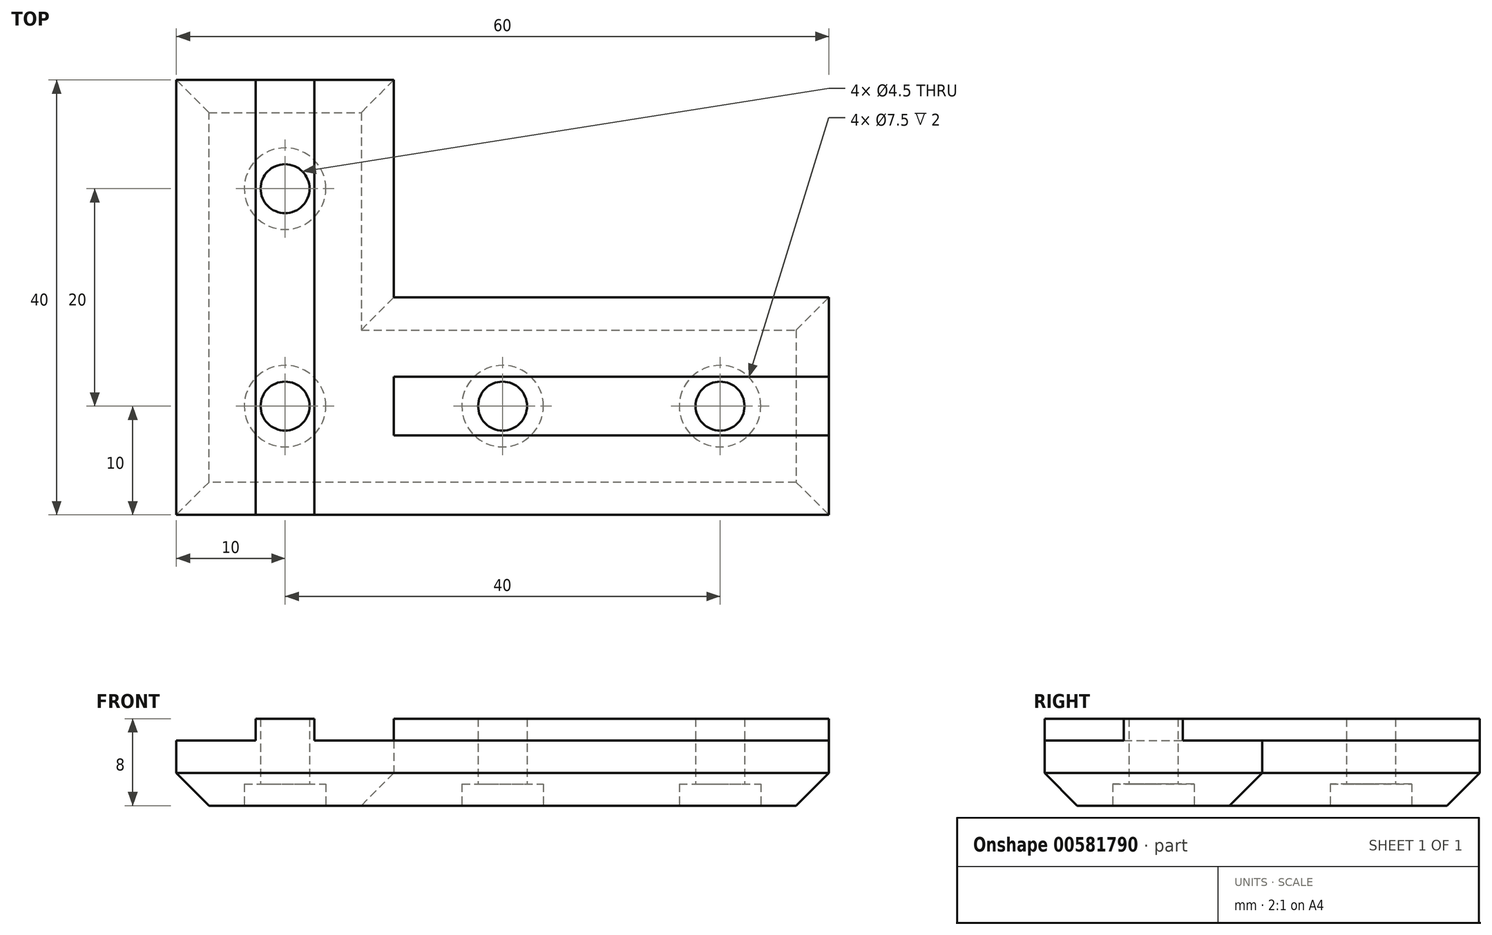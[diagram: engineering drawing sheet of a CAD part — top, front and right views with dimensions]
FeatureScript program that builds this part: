
annotation { "Feature Type Name" : "Feature", "Feature Type Description" : "" }
export const myFeature = defineFeature(function(context is Context, id is Id, definition is map)
    precondition{}
    {
        {
            var Q0;
            Q0=qCreatedBy(makeId("Top.planeOp"),FACE);
            var sketch = newSketch(context, id + "F0", { "sketchPlane" : qUnion([Q0])});
            skLineSegment(sketch, "E0", {"start": v(0, 0) * mm, "end": v(0, 40) * mm});
            skLineSegment(sketch, "E1", {"start": v(0, 40) * mm, "end": v(20, 40) * mm});
            skLineSegment(sketch, "E2", {"start": v(20, 40) * mm, "end": v(20, 20) * mm});
            skLineSegment(sketch, "E3", {"start": v(20, 20) * mm, "end": v(60, 20) * mm});
            skLineSegment(sketch, "E4", {"start": v(60, 20) * mm, "end": v(60, 0) * mm});
            skLineSegment(sketch, "E5", {"start": v(60, 0) * mm, "end": v(0, 0) * mm});
            skSolve(sketch);
        }
        {
            var Q0;
            Q0=qSketchRegion(id+"F0",true);
            extrude(context, id + "F1", {"entities" : qUnion([Q0]), "depth" : 6 * mm});
        }
        {
            var Q0;
            Q0=makeQuery(id+"F1.opExtrude","CAP_FACE",FACE,{"disambiguationData":[OSD([sQuery(id+"F0.wireOp",EDGE,"E0"),sQuery(id+"F0.wireOp",EDGE,"E1"),sQuery(id+"F0.wireOp",EDGE,"E2"),sQuery(id+"F0.wireOp",EDGE,"E3"),sQuery(id+"F0.wireOp",EDGE,"E4"),sQuery(id+"F0.wireOp",EDGE,"E5")])],"isStart":false});
            var sketch = newSketch(context, id + "F2", { "sketchPlane" : qUnion([Q0])});
            skLineSegment(sketch, "E6", {"start": v(7.3, 40) * mm, "end": v(12.71, 40) * mm});
            skLineSegment(sketch, "E7", {"start": v(12.71, 40) * mm, "end": v(12.71, 0) * mm});
            skLineSegment(sketch, "E8", {"start": v(12.71, 0) * mm, "end": v(10, 0) * mm});
            skPoint(sketch, "E8.endSnap0", {"position": v(10, 40) * mm});
            skLineSegment(sketch, "E9", {"start": v(10, 0) * mm, "end": v(7.3, 0) * mm});
            skLineSegment(sketch, "E10", {"start": v(7.3, 0) * mm, "end": v(7.3, 40) * mm});
            skLineSegment(sketch, "E11", {"start": v(60, 12.7) * mm, "end": v(60, 7.3) * mm});
            skLineSegment(sketch, "E12", {"start": v(60, 7.3) * mm, "end": v(20, 7.3) * mm});
            skLineSegment(sketch, "E13", {"start": v(20, 7.3) * mm, "end": v(20, 10) * mm});
            skPoint(sketch, "E13.endSnap0", {"position": v(60, 10) * mm});
            skLineSegment(sketch, "E14", {"start": v(20, 10) * mm, "end": v(20, 12.71) * mm});
            skLineSegment(sketch, "E15", {"start": v(20, 12.71) * mm, "end": v(60, 12.71) * mm});
            skSolve(sketch);
        }
        {
            var Q0;
            Q0=qSketchRegion(id+"F2",true);
            extrude(context, id + "F3", {"entities" : qUnion([Q0]), "operationType" : NewBodyOperationType.ADD, "depth" : 2 * mm});
        }
        {
            var Q0;
            Q0=makeQuery(id+"F1.opExtrude","CAP_FACE",FACE,{"disambiguationData":[OSD([sQuery(id+"F0.wireOp",EDGE,"E0"),sQuery(id+"F0.wireOp",EDGE,"E1"),sQuery(id+"F0.wireOp",EDGE,"E2"),sQuery(id+"F0.wireOp",EDGE,"E3"),sQuery(id+"F0.wireOp",EDGE,"E4"),sQuery(id+"F0.wireOp",EDGE,"E5")])],"isStart":true});
            var sketch = newSketch(context, id + "F4", { "sketchPlane" : qUnion([Q0])});
            skCircle(sketch, "E16", {"center": v(10, -10) * mm, "radius": 2.25 * mm});
            skCircle(sketch, "E17", {"center": v(50, -10) * mm, "radius": 2.25 * mm});
            skCircle(sketch, "E18", {"center": v(10, -30) * mm, "radius": 2.25 * mm});
            skCircle(sketch, "E19", {"center": v(30, -10) * mm, "radius": 2.25 * mm});
            skSolve(sketch);
        }
        {
            var Q0;
            Q0=qSketchRegion(id+"F4",true);
            extrude(context, id + "F5", {"entities" : qUnion([Q0]), "operationType" : NewBodyOperationType.REMOVE, "endBound" : BoundingType.THROUGH_ALL, "oppositeDirection" : true, "depth" : 25 * mm});
        }
        {
            var Q0;
            Q0=makeQuery(id+"F1.opExtrude","CAP_FACE",FACE,{"disambiguationData":[OSD([sQuery(id+"F0.wireOp",EDGE,"E0"),sQuery(id+"F0.wireOp",EDGE,"E1"),sQuery(id+"F0.wireOp",EDGE,"E2"),sQuery(id+"F0.wireOp",EDGE,"E3"),sQuery(id+"F0.wireOp",EDGE,"E4"),sQuery(id+"F0.wireOp",EDGE,"E5")])],"isStart":true});
            var sketch = newSketch(context, id + "F6", { "sketchPlane" : qUnion([Q0])});
            skCircle(sketch, "E20", {"center": v(10, -10) * mm, "radius": 3.75 * mm});
            skCircle(sketch, "E21", {"center": v(30, -10) * mm, "radius": 3.75 * mm});
            skCircle(sketch, "E22", {"center": v(50, -10) * mm, "radius": 3.75 * mm});
            skCircle(sketch, "E23", {"center": v(10, -30) * mm, "radius": 3.75 * mm});
            skSolve(sketch);
        }
        {
            var Q0;
            Q0=qSketchRegion(id+"F6",true);
            extrude(context, id + "F7", {"entities" : qUnion([Q0]), "operationType" : NewBodyOperationType.REMOVE, "oppositeDirection" : true, "depth" : 2 * mm});
        }
        {
            var Q0;
            Q0=makeQuery(id+"F1.opExtrude","CAP_EDGE",EDGE,{"disambiguationData":[OSD([sQuery(id+"F0.wireOp",EDGE,"E5")])],"isStart":true});
            var Q1;
            Q1=makeQuery(id+"F1.opExtrude","CAP_EDGE",EDGE,{"disambiguationData":[OSD([sQuery(id+"F0.wireOp",EDGE,"E0")])],"isStart":true});
            var Q2;
            Q2=makeQuery(id+"F1.opExtrude","CAP_EDGE",EDGE,{"disambiguationData":[OSD([sQuery(id+"F0.wireOp",EDGE,"E2")])],"isStart":true});
            var Q3;
            Q3=makeQuery(id+"F1.opExtrude","CAP_EDGE",EDGE,{"disambiguationData":[OSD([sQuery(id+"F0.wireOp",EDGE,"E3")])],"isStart":true});
            var Q4;
            Q4=makeQuery(id+"F1.opExtrude","CAP_EDGE",EDGE,{"disambiguationData":[OSD([sQuery(id+"F0.wireOp",EDGE,"E4")])],"isStart":true});
            var Q5;
            Q5=makeQuery(id+"F1.opExtrude","CAP_EDGE",EDGE,{"disambiguationData":[OSD([sQuery(id+"F0.wireOp",EDGE,"E1")])],"isStart":true});
            chamfer(context, id + "F8", {"entities" : qUnion([Q0, Q1, Q2, Q3, Q4, Q5]), "width" : 3 * mm, "tangentPropagation" : true});
        }
    });
